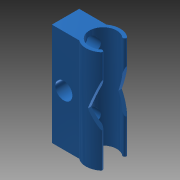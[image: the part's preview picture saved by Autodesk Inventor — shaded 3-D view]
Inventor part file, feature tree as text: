
AUTODESK INVENTOR PART (.ipt)
format: ipt  version: 2013 (Build 170138000, 138)  size: 162,304 bytes
history: native  units: mm
features: extrude x4, sketch x3, fillet x1
ambient origin geometry x8: Origin, YZ Plane, XZ Plane, XY Plane, X Axis, Y Axis, Z Axis, Center Point
bodies: Solid1 (feature_tree)
feature tree (8):
  extrude  "Extrusion1"  Depth=10.0mm
  extrude  "Extrusion2"  Depth=30.0mm TaperAngle=0.0deg
  fillet  "Fillet1"  Radius=3.0mm
  extrude  "Extrusion3"  Depth=3.0mm
  extrude  "Extrusion4"  Depth=18.0mm
  sketch  "Sketch1"  dims[d0=8.0mm d1=10.0mm]
  sketch  "Sketch3"  dims[d3=6.0mm d4=30.0mm d5=0.0mm d6=3.0mm]
  sketch  "Sketch4"  dims[d7=10.0mm d8=0.0mm d9=3.0mm d10=18.0mm d12=0.5mm d14=5.0mm d15=10.0mm d16=0.0mm d17=19.198622mm d18=22.68928mm d19=8.0mm d20=5.0mm d21=5.0mm d22=7.0mm d23=0.0mm d24=11.0mm d25=1.0mm d26=1.0mm]
